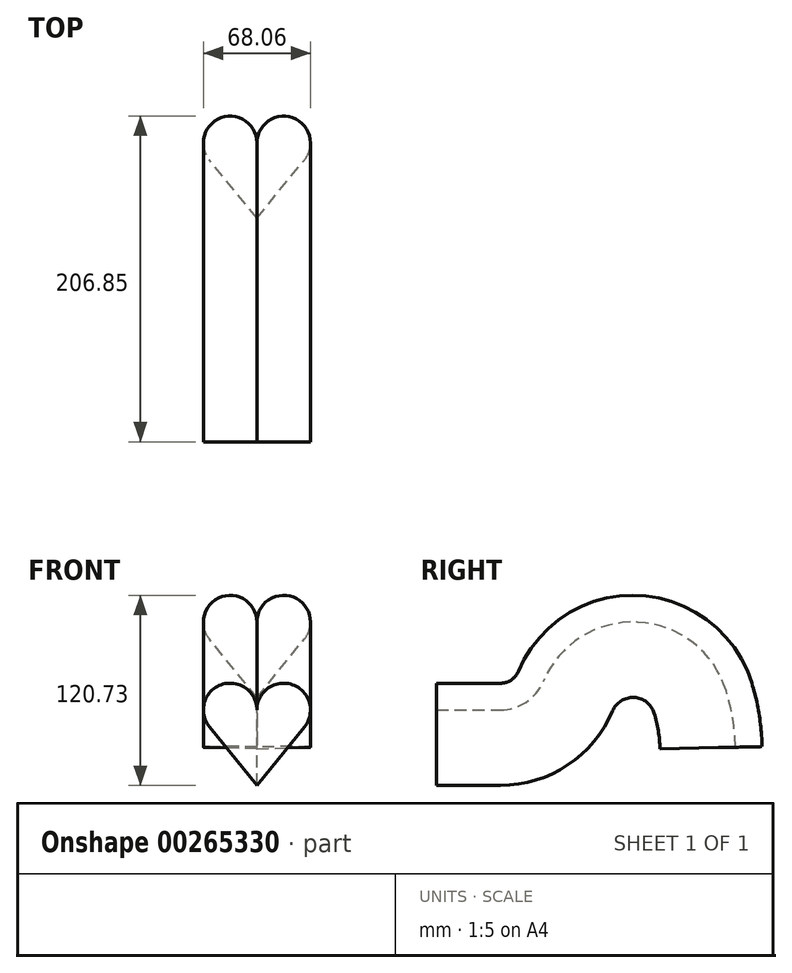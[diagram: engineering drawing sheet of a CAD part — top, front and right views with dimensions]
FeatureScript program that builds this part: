
annotation { "Feature Type Name" : "Feature", "Feature Type Description" : "" }
export const myFeature = defineFeature(function(context is Context, id is Id, definition is map)
    precondition{}
    {
        {
            var Q0;
            Q0=qCreatedBy(makeId("Front.planeOp"),FACE);
            var sketch = newSketch(context, id + "F0", { "sketchPlane" : qUnion([Q0])});
            skArc(sketch, "E0", {"start": v(0, 10.74) * mm, "mid": v(-22.71, 26.77) * mm, "end": v(-30.21, 0) * mm});
            skArc(sketch, "E1.MirrorC", {"start": v(0, 10.74) * mm, "mid": v(22.71, 26.77) * mm, "end": v(30.21, 0) * mm});
            skLineSegment(sketch, "E2", {"start": v(0, -37.13) * mm, "end": v(-30.21, 0) * mm});
            skLineSegment(sketch, "E3", {"start": v(0, -37.13) * mm, "end": v(30.21, 0) * mm});
            skSolve(sketch);
        }
        {
            var Q0;
            Q0=qCreatedBy(makeId("Right.planeOp"),FACE);
            var sketch = newSketch(context, id + "F1", { "sketchPlane" : qUnion([Q0])});
            skLineSegment(sketch, "E4", {"start": v(0, 0) * mm, "end": v(40.64, 0) * mm});
            skArc(sketch, "E5", {"start": v(40.64, 0) * mm, "mid": v(62.83, 6.7) * mm, "end": v(77.62, 24.53) * mm});
            skArc(sketch, "E6", {"start": v(77.62, 24.53) * mm, "mid": v(127.4, 55.78) * mm, "end": v(173.79, 19.69) * mm});
            skArc(sketch, "E7", {"start": v(173.79, 19.69) * mm, "mid": v(177.58, 3.46) * mm, "end": v(179.1, -13.14) * mm});
            skSolve(sketch);
        }
        {
            var Q0;
            Q0=makeQuery(id+"F0.imprint","IMPRINT",FACE,{"disambiguationData":[TD([[makeQuery(id+"F0.imprint","IMPRINT",EDGE,{"derivedFrom":sQuery(id+"F0.wireOp",EDGE,"E0")}),1.0]])]});
            var Q1;
            Q1=sQuery(id+"F1.wireOp",EDGE,"E4");
            var Q2;
            Q2=sQuery(id+"F1.wireOp",EDGE,"E5");
            var Q3;
            Q3=sQuery(id+"F1.wireOp",EDGE,"E6");
            var Q4;
            Q4=sQuery(id+"F1.wireOp",EDGE,"E7");
            sweep(context, id + "F2", {"profiles" : qUnion([Q0]), "path" : qUnion([Q1, Q2, Q3, Q4])});
        }
    });
